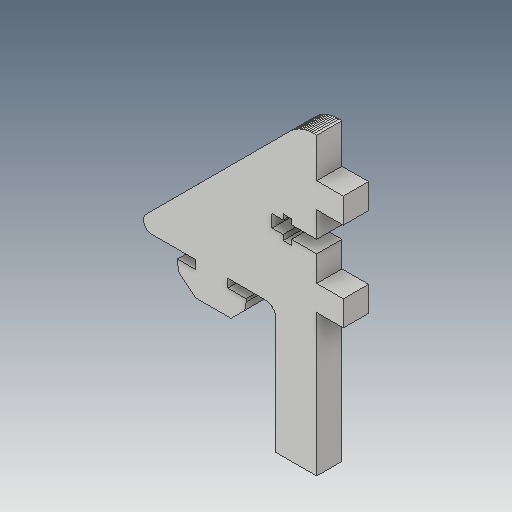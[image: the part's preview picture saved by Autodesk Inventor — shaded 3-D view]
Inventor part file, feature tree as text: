
AUTODESK INVENTOR PART (.ipt)
format: ipt  version: 2017 (Build 210142000, 142)  size: 363,008 bytes
history: native  units: mm
features: other x3, sketch x1
ambient origin geometry x8: Origin, YZ Plane, XZ Plane, XY Plane, X Axis, Y Axis, Z Axis, Center Point
bodies: Solid1 (feature_tree)
feature tree (4):
  other  "Y-Motor-Brace.ipt"
  other  "Solid1::Y-Motor-Brace.ipt"
  other  "TaggingFeature1"
  sketch  "Sketch1"  dims[d0=10.0mm]
